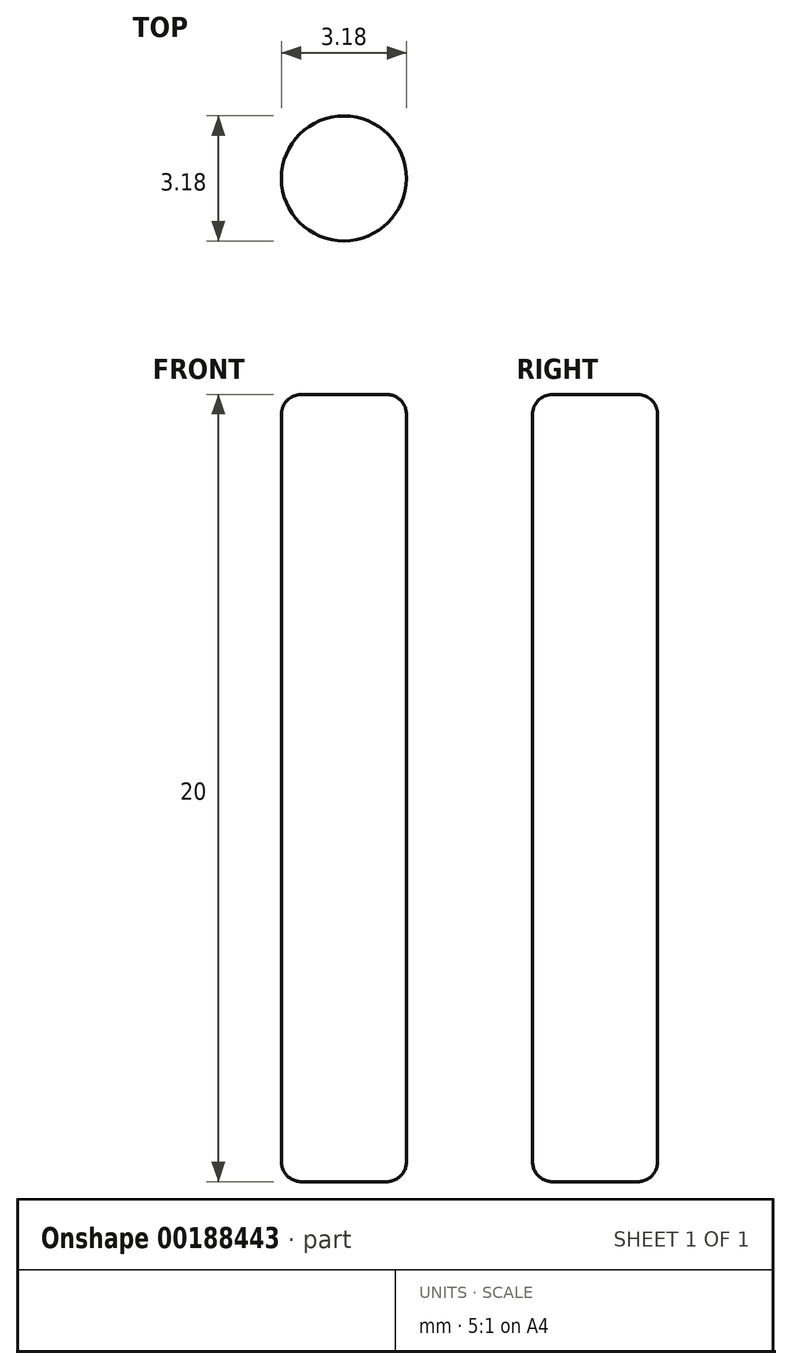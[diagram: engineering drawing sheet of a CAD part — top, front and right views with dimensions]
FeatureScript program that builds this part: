
annotation { "Feature Type Name" : "Feature", "Feature Type Description" : "" }
export const myFeature = defineFeature(function(context is Context, id is Id, definition is map)
    precondition{}
    {
        {
            var Q0;
            Q0=qCreatedBy(makeId("Top.planeOp"),FACE);
            var sketch = newSketch(context, id + "F0", { "sketchPlane" : qUnion([Q0])});
            skCircle(sketch, "E0", {"center": v(0, 0) * mm, "radius": 1.59 * mm});
            skSolve(sketch);
        }
        {
            var Q0;
            Q0 = qSketchRegion(id + "F0", true);
            extrude(context, id + "F1", {"entities" : qUnion([Q0]), "depth" : 20 * mm, "offsetDistance" : 25 * mm});
        }
        {
            var Q0;
            Q0=makeQuery(id+"F1.opExtrude","CAP_EDGE",EDGE,{"disambiguationData":[OSD([sQuery(id+"F0.wireOp",EDGE,"E0")])],"isStart":false});
            var Q1;
            Q1=makeQuery(id+"F1.opExtrude","CAP_EDGE",EDGE,{"disambiguationData":[OSD([sQuery(id+"F0.wireOp",EDGE,"E0")])],"isStart":true});
            fillet(context, id + "F2", {"entities" : qUnion([Q0, Q1]), "radius" : .5 * mm, "tangentPropagation" : true, "allowEdgeOverflow" : false});
        }
    });
